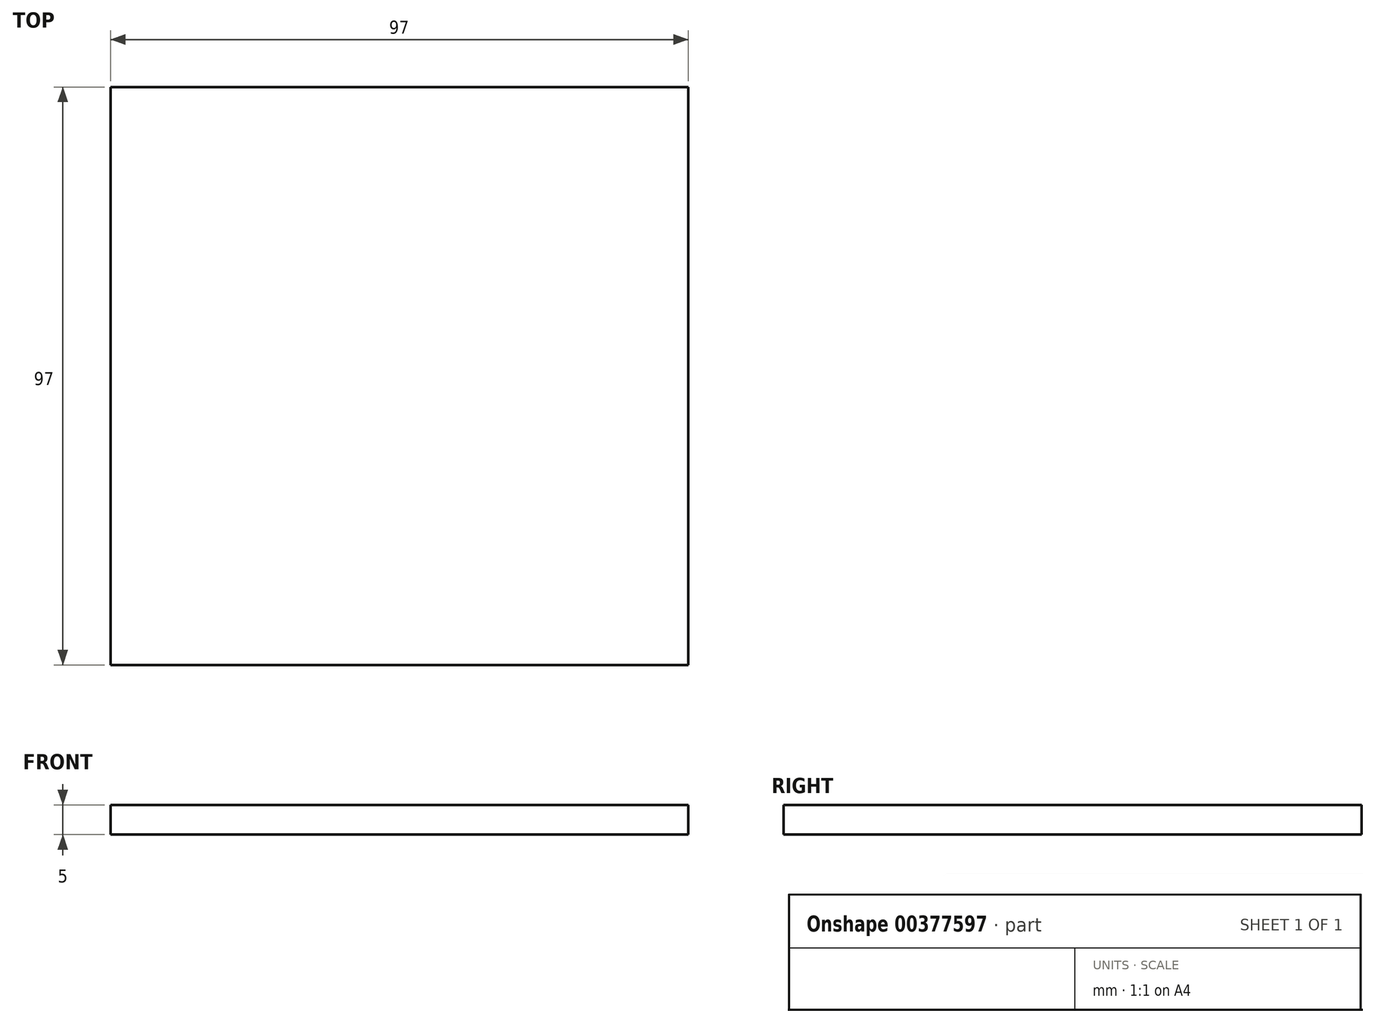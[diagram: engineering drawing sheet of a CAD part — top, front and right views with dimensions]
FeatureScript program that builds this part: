
annotation { "Feature Type Name" : "Feature", "Feature Type Description" : "" }
export const myFeature = defineFeature(function(context is Context, id is Id, definition is map)
    precondition{}
    {
        {
            var Q0;
            Q0=qCreatedBy(makeId("Top.planeOp"),FACE);
            var sketch = newSketch(context, id + "F0", { "sketchPlane" : qUnion([Q0])});
            skLineSegment(sketch, "E0.bottom", {"start": v(-48.5, 48.5) * mm, "end": v(48.5, 48.5) * mm});
            skLineSegment(sketch, "E0.top", {"start": v(-48.5, -48.5) * mm, "end": v(48.5, -48.5) * mm});
            skLineSegment(sketch, "E0.left", {"start": v(-48.5, 48.5) * mm, "end": v(-48.5, -48.5) * mm});
            skLineSegment(sketch, "E0.right", {"start": v(48.5, 48.5) * mm, "end": v(48.5, -48.5) * mm});
            skPoint(sketch, "E0.middle", {"position": v(0, 0) * mm});
            skSolve(sketch);
        }
        {
            var Q0;
            Q0 = qSketchRegion(id + "F0", true);
            extrude(context, id + "F1", {"entities" : qUnion([Q0]), "depth" : 5 * mm});
        }
    });
